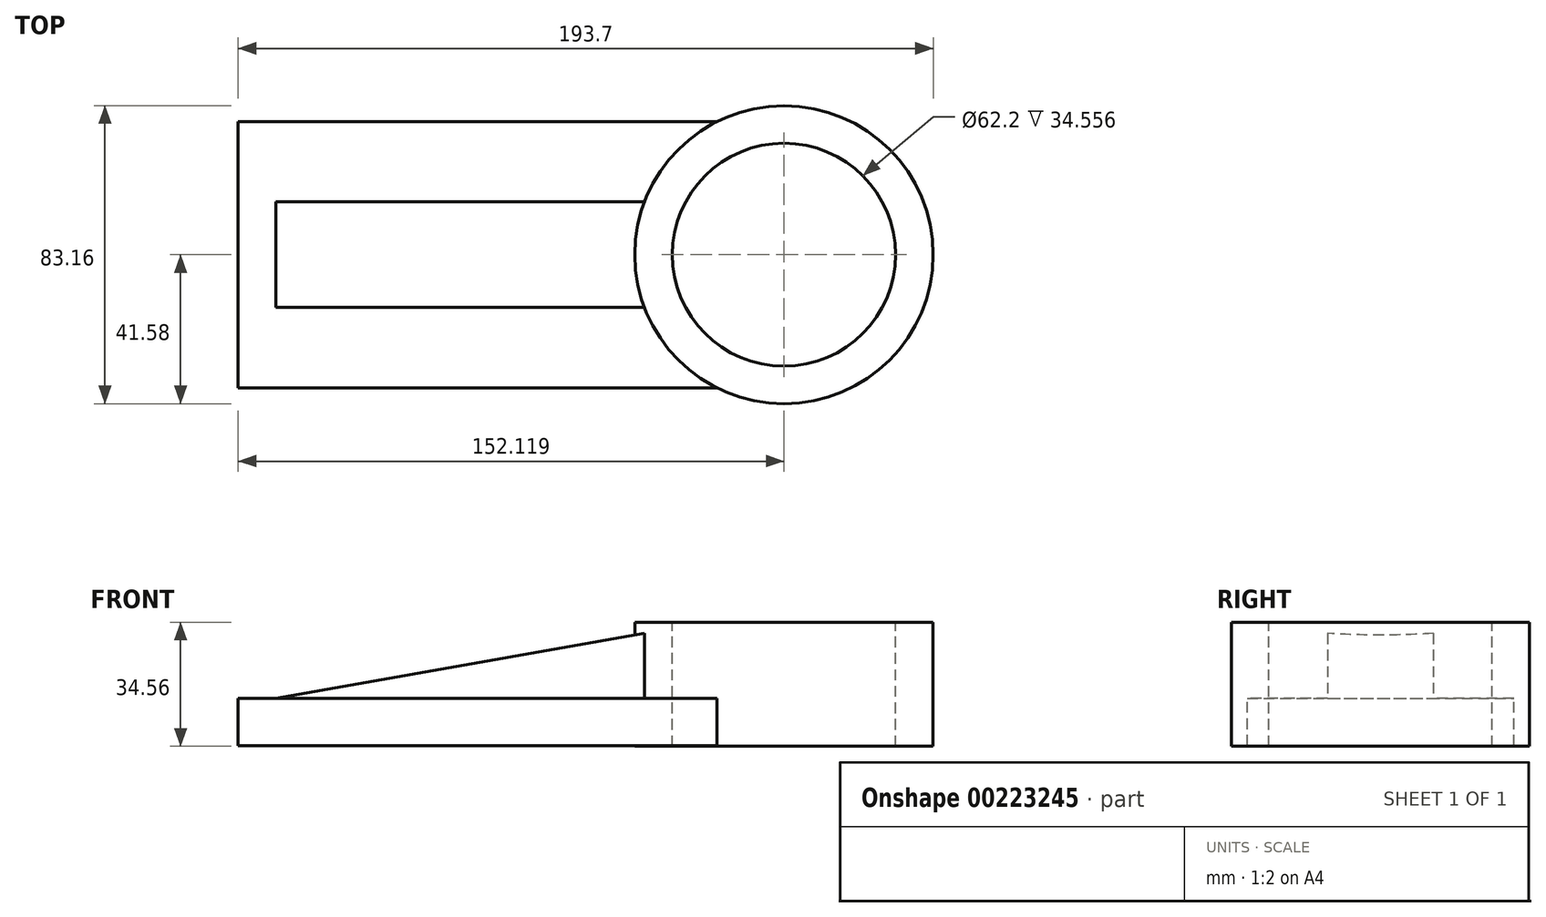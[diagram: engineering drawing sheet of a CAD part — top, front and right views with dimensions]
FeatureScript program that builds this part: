
annotation { "Feature Type Name" : "Feature", "Feature Type Description" : "" }
export const myFeature = defineFeature(function(context is Context, id is Id, definition is map)
    precondition{}
    {
        {
            var Q0;
            Q0=qCreatedBy(makeId("Top.planeOp"),FACE);
            var sketch = newSketch(context, id + "F6", { "sketchPlane" : qUnion([Q0])});
            skLineSegment(sketch, "E0.bottom", {"start": v(76.06, -37.14) * mm, "end": v(-76.06, -37.14) * mm});
            skLineSegment(sketch, "E0.top", {"start": v(76.06, 37.14) * mm, "end": v(-76.06, 37.14) * mm});
            skLineSegment(sketch, "E0.left", {"start": v(76.06, -37.14) * mm, "end": v(76.06, 37.14) * mm});
            skLineSegment(sketch, "E0.right", {"start": v(-76.06, -37.14) * mm, "end": v(-76.06, 37.14) * mm});
            skPoint(sketch, "E0.middle", {"position": v(0, 0) * mm});
            skSolve(sketch);
        }
        {
            var Q0;
            Q0=makeQuery(id+"F6.imprint","IMPRINT",FACE,{"disambiguationData":[TD([[makeQuery(id+"F6.imprint","IMPRINT",EDGE,{"derivedFrom":sQuery(id+"F6.wireOp",EDGE,"E0.bottom")}),-1.0]])]});
            extrude(context, id + "F0", {"entities" : qUnion([Q0]), "depth" : 13.2 * mm});
        }
        {
            var Q0;
            Q0=makeQuery(id+"F0.opExtrude","CAP_FACE",FACE,{"disambiguationData":[OSD([sQuery(id+"F6.wireOp",EDGE,"E0.bottom"),sQuery(id+"F6.wireOp",EDGE,"E0.top"),sQuery(id+"F6.wireOp",EDGE,"E0.left"),sQuery(id+"F6.wireOp",EDGE,"E0.right")])],"isStart":false});
            var sketch = newSketch(context, id + "F7", { "sketchPlane" : qUnion([Q0])});
            skCircle(sketch, "E1", {"center": v(76.06, 0) * mm, "radius": 41.58 * mm});
            skSolve(sketch);
        }
        {
            var Q0;
            {var subQ5=makeQuery(id+"F0.opExtrude","CAP_EDGE",EDGE,{"disambiguationData":[OSD([sQuery(id+"F6.wireOp",EDGE,"E0.left")])],"isStart":false});Q0=makeQuery(id+"F7.imprint","IMPRINT",FACE,{"disambiguationData":[TD([[makeQuery(id+"F7.imprint","IMPRINT",EDGE,{"derivedFrom":subQ5}),1.0]])]});}
            var Q1;
            {var subQ5=makeQuery(id+"F0.opExtrude","CAP_EDGE",EDGE,{"disambiguationData":[OSD([sQuery(id+"F6.wireOp",EDGE,"E0.left")])],"isStart":false});Q1=makeQuery(id+"F7.imprint","IMPRINT",FACE,{"disambiguationData":[TD([[makeQuery(id+"F7.imprint","IMPRINT",EDGE,{"derivedFrom":subQ5}),-1.0]])]});}
            extrude(context, id + "F1", {"entities" : qUnion([Q0, Q1]), "operationType" : NewBodyOperationType.ADD, "oppositeDirection" : true, "depth" : 13.36 * mm});
        }
        {
            var Q0;
            Q0=makeQuery(id+"F1.boolean.opBoolean","MERGE",FACE,{"derivedFrom":[makeQuery(id+"F0.opExtrude","CAP_FACE",FACE,{"disambiguationData":[OSD([sQuery(id+"F6.wireOp",EDGE,"E0.bottom"),sQuery(id+"F6.wireOp",EDGE,"E0.top"),sQuery(id+"F6.wireOp",EDGE,"E0.left"),sQuery(id+"F6.wireOp",EDGE,"E0.right")])],"isStart":false}),makeQuery(id+"F1.opExtrude","CAP_FACE",FACE,{"disambiguationData":[OSD([sQuery(id+"F7.wireOp",EDGE,"E1")])],"isStart":true})]});
            var sketch = newSketch(context, id + "F2", { "sketchPlane" : qUnion([Q0])});
            skLineSegment(sketch, "E2.bottom", {"start": v(75.64, 14.75) * mm, "end": v(-75.64, 14.75) * mm});
            skLineSegment(sketch, "E2.top", {"start": v(75.64, -14.75) * mm, "end": v(-75.64, -14.75) * mm});
            skLineSegment(sketch, "E2.left", {"start": v(75.64, 14.75) * mm, "end": v(75.64, -14.75) * mm});
            skLineSegment(sketch, "E2.right", {"start": v(-75.64, 14.75) * mm, "end": v(-75.64, -14.75) * mm});
            skPoint(sketch, "E2.middle", {"position": v(0, 0) * mm});
            skSolve(sketch);
        }
        {
            var Q0;
            Q0=makeQuery(id+"F2.imprint","IMPRINT",FACE,{"disambiguationData":[TD([[makeQuery(id+"F2.imprint","IMPRINT",EDGE,{"derivedFrom":sQuery(id+"F2.wireOp",EDGE,"E2.bottom")}),1.0]])]});
            extrude(context, id + "F8", {"entities" : qUnion([Q0]), "operationType" : NewBodyOperationType.ADD, "depth" : 20.62 * mm});
        }
        {
            var Q0;
            Q0=makeQuery(id+"F8.opExtrude","CAP_EDGE",EDGE,{"disambiguationData":[OSD([sQuery(id+"F2.wireOp",EDGE,"E2.right")])],"isStart":false});
            chamfer(context, id + "F3", {"entities" : qUnion([Q0]), "chamferType" : ChamferType.OFFSET_ANGLE, "width" : 127 * mm, "oppositeDirection" : false, "angle" : 10 * degree, "tangentPropagation" : true});
        }
        {
            var Q0;
            Q0=makeQuery(id+"F1.opExtrude","CAP_FACE",FACE,{"disambiguationData":[OSD([sQuery(id+"F7.wireOp",EDGE,"E1")])],"isStart":false});
            extrude(context, id + "F4", {"entities" : qUnion([Q0]), "operationType" : NewBodyOperationType.ADD, "oppositeDirection" : true, "depth" : 34.56 * mm});
        }
        {
            var Q0;
            Q0=makeQuery(id+"F4.opExtrude","CAP_FACE",FACE,{"disambiguationData":[OSD([sQuery(id+"F7.wireOp",EDGE,"E1")])],"isStart":false});
            var sketch = newSketch(context, id + "F5", { "sketchPlane" : qUnion([Q0])});
            skCircle(sketch, "E3", {"center": v(76.06, 0) * mm, "radius": 31.1 * mm});
            skSolve(sketch);
        }
        {
            var Q0;
            Q0=makeQuery(id+"F5.imprint","IMPRINT",FACE,{"disambiguationData":[TD([[makeQuery(id+"F5.imprint","IMPRINT",EDGE,{"derivedFrom":sQuery(id+"F5.wireOp",EDGE,"E3")}),1.0]])]});
            extrude(context, id + "F9", {"entities" : qUnion([Q0]), "operationType" : NewBodyOperationType.REMOVE, "endBound" : BoundingType.THROUGH_ALL, "oppositeDirection" : true, "depth" : 25.4 * mm});
        }
    });
